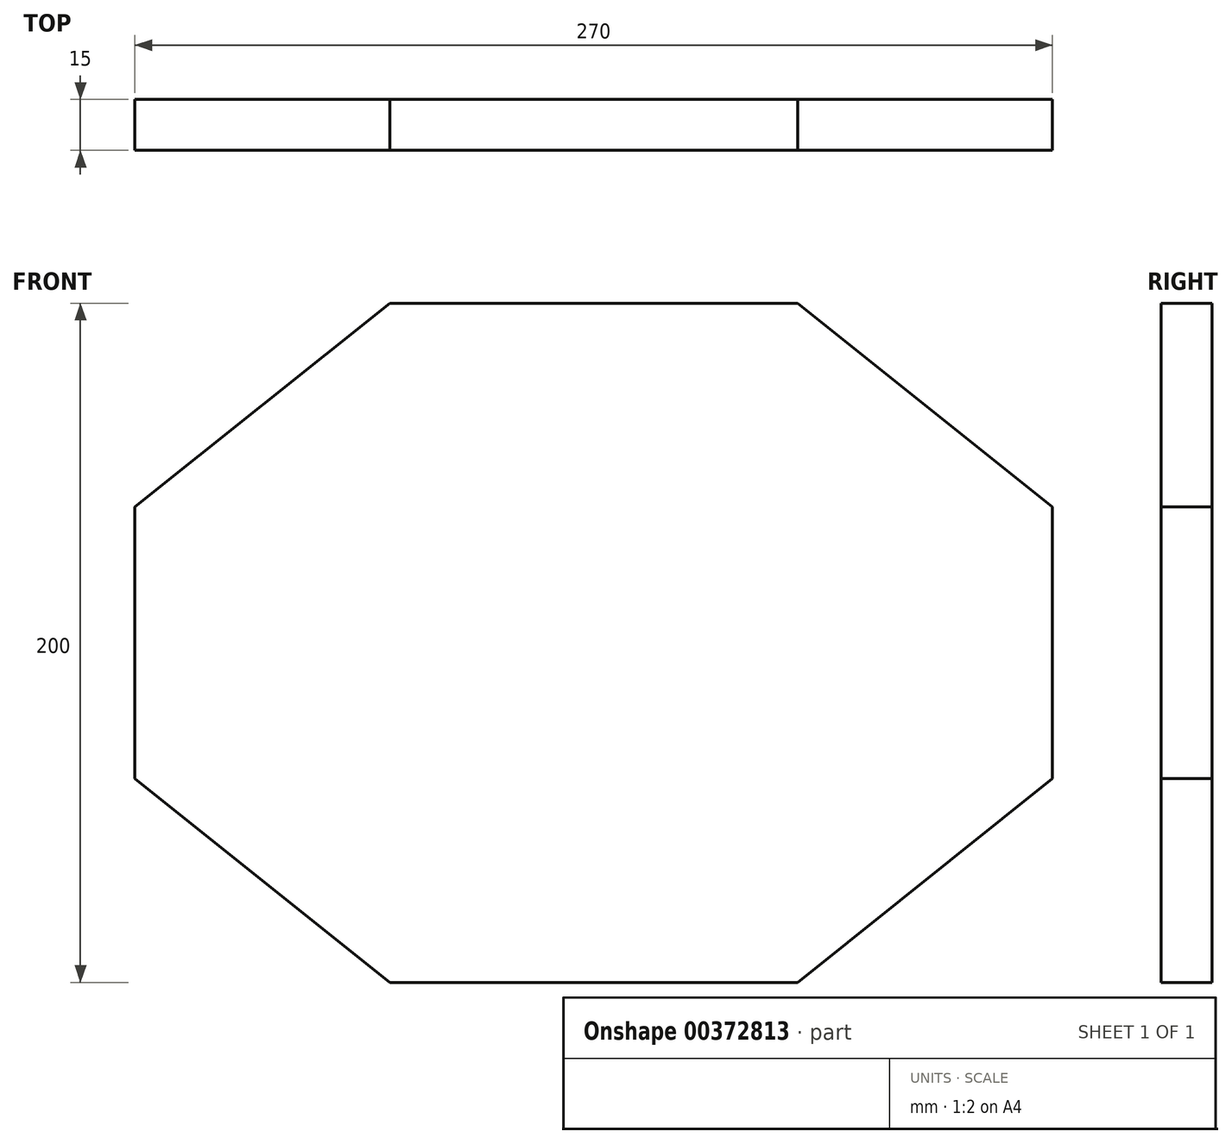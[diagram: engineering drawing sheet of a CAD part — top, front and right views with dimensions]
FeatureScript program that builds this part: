
annotation { "Feature Type Name" : "Feature", "Feature Type Description" : "" }
export const myFeature = defineFeature(function(context is Context, id is Id, definition is map)
    precondition{}
    {
        {
            var Q0;
            Q0=qCreatedBy(makeId("Front.planeOp"),FACE);
            var sketch = newSketch(context, id + "F0", { "sketchPlane" : qUnion([Q0])});
            skLineSegment(sketch, "E0", {"start": v(-135, 0) * mm, "end": v(-135, 40) * mm});
            skLineSegment(sketch, "E1", {"start": v(-135, 40) * mm, "end": v(-60, 100) * mm});
            skLineSegment(sketch, "E2", {"start": v(-60, 100) * mm, "end": v(0, 100) * mm});
            skLineSegment(sketch, "E3.MirrorCS", {"start": v(135, 40) * mm, "end": v(60, 100) * mm});
            skLineSegment(sketch, "E4.MirrorCS", {"start": v(60, 100) * mm, "end": v(0, 100) * mm});
            skLineSegment(sketch, "E5.MirrorCS", {"start": v(135, 0) * mm, "end": v(135, 40) * mm});
            skLineSegment(sketch, "E6.MirrorCS", {"start": v(-135, 0) * mm, "end": v(-135, -40) * mm});
            skLineSegment(sketch, "E7.MirrorCS", {"start": v(-135, -40) * mm, "end": v(-60, -100) * mm});
            skLineSegment(sketch, "E8.MirrorCS", {"start": v(-60, -100) * mm, "end": v(0, -100) * mm});
            skLineSegment(sketch, "E9.MirrorCS", {"start": v(60, -100) * mm, "end": v(0, -100) * mm});
            skLineSegment(sketch, "E10.MirrorCS", {"start": v(135, -40) * mm, "end": v(60, -100) * mm});
            skLineSegment(sketch, "E11.MirrorCS", {"start": v(135, 0) * mm, "end": v(135, -40) * mm});
            skSolve(sketch);
        }
        {
            var Q0;
            Q0 = qSketchRegion(id + "F0", true);
            extrude(context, id + "F1", {"entities" : qUnion([Q0]), "endBound" : BoundingType.SYMMETRIC, "depth" : 15 * mm});
        }
    });
